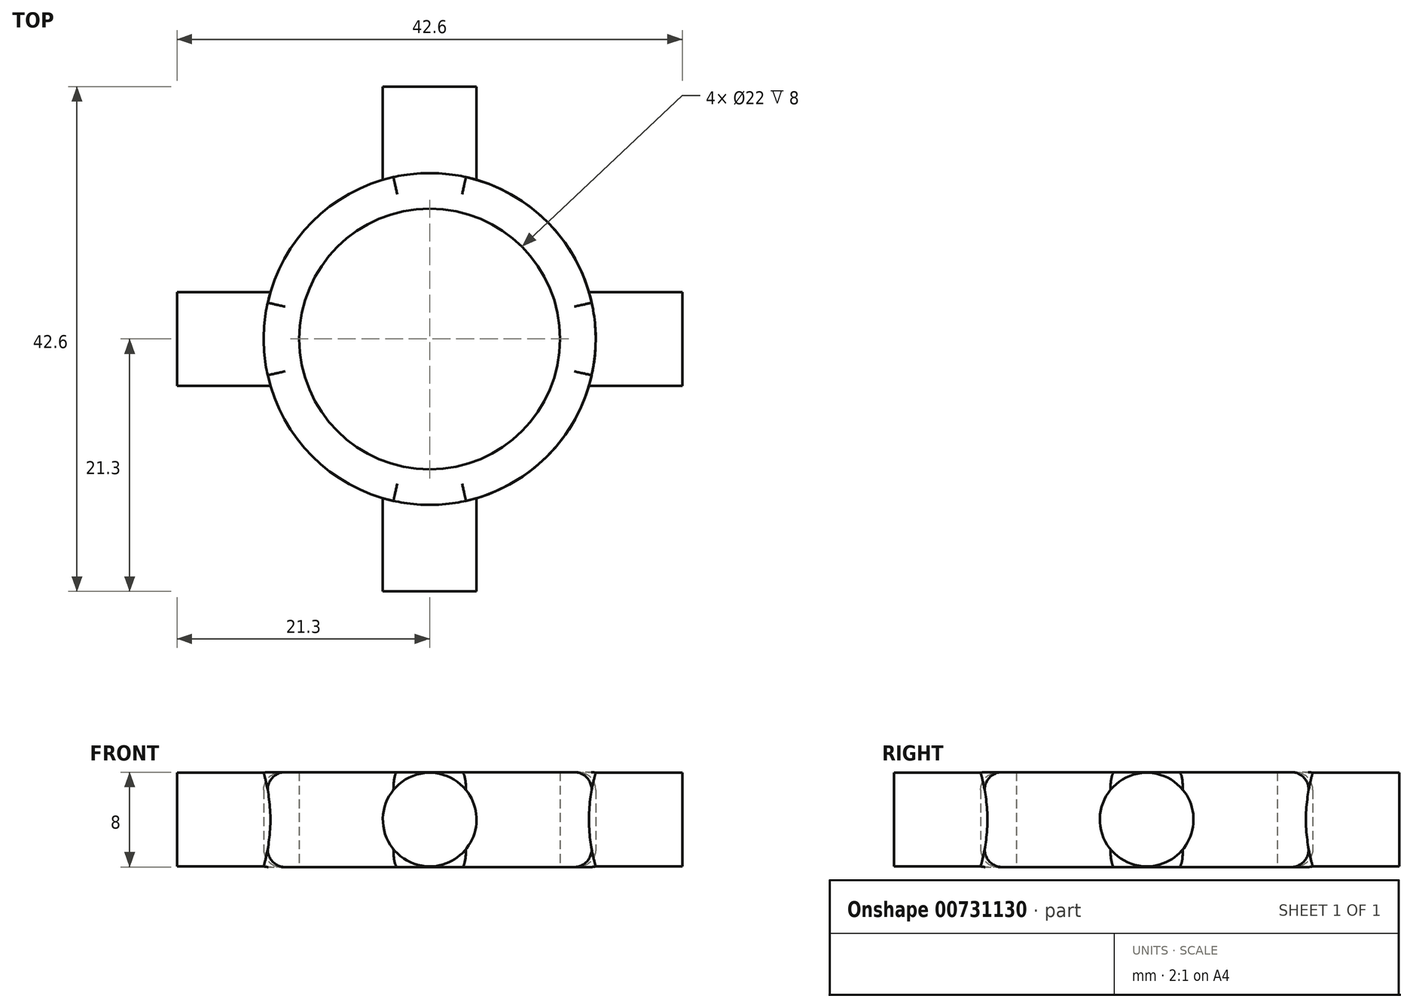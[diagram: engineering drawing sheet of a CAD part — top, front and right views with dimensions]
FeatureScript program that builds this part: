
annotation { "Feature Type Name" : "Feature", "Feature Type Description" : "" }
export const myFeature = defineFeature(function(context is Context, id is Id, definition is map)
    precondition{}
    {
        {
            var Q0;
            Q0=qCreatedBy(makeId("Top.planeOp"),FACE);
            var sketch = newSketch(context, id + "F0", { "sketchPlane" : qUnion([Q0])});
            skCircle(sketch, "E0", {"center": v(0, 0) * mm, "radius": 11 * mm});
            skCircle(sketch, "E1.0", {"center": v(0, 0) * mm, "radius": 14 * mm});
            skSolve(sketch);
        }
        {
            var Q0;
            Q0=qCreatedBy(makeId("Right.planeOp"),FACE);
            cPlane(context, id + "F1", {"entities" : qUnion([Q0]), "cplaneType" : CPlaneType.OFFSET, "offset" : 13.3 * mm, "width" : 150 * mm, "height" : 150 * mm});
        }
        {
            var Q0;
            Q0=qCreatedBy(id+"F1.planeOp",FACE);
            var sketch = newSketch(context, id + "F2", { "sketchPlane" : qUnion([Q0])});
            skCircle(sketch, "E2", {"center": v(0, 0) * mm, "radius": 3.95 * mm});
            skSolve(sketch);
        }
        {
            var Q0;
            Q0=makeQuery(id+"F0.imprint","IMPRINT",FACE,{"disambiguationData":[TD([[makeQuery(id+"F0.imprint","IMPRINT",EDGE,{"derivedFrom":sQuery(id+"F0.wireOp",EDGE,"E0")}),-1.0]])]});
            extrude(context, id + "F3", {"entities" : qUnion([Q0]), "endBound" : BoundingType.SYMMETRIC, "depth" : 8 * mm, "offsetDistance" : 25 * mm});
        }
        {
            var Q0;
            Q0=qSketchRegion(id+"F2",true);
            extrude(context, id + "F4", {"entities" : qUnion([Q0]), "operationType" : NewBodyOperationType.ADD, "depth" : 8 * mm, "offsetDistance" : 25 * mm});
        }
        {
            var Q0;
            Q0=makeQuery(id+"F3.opExtrude","CAP_EDGE",EDGE,{"disambiguationData":[OSD([sQuery(id+"F0.wireOp",EDGE,"E1.0")])],"isStart":false});
            var Q1;
            Q1=makeQuery(id+"F3.opExtrude","CAP_EDGE",EDGE,{"disambiguationData":[OSD([sQuery(id+"F0.wireOp",EDGE,"E1.0")])],"isStart":true});
            fillet(context, id + "F5", {"entities" : qUnion([Q0, Q1]), "radius" : 1.5 * mm, "tangentPropagation" : true, "allowEdgeOverflow" : false});
        }
        {
            var Q0;
            Q0=makeQuery(id+"F3.opExtrude","SWEPT_BODY",BODY,{"disambiguationData":[OSD([sQuery(id+"F0.wireOp",EDGE,"E0"),sQuery(id+"F0.wireOp",EDGE,"E1.0")])]});
            var Q1;
            Q1=makeQuery(id+"F3.opExtrude","CAP_EDGE",EDGE,{"disambiguationData":[OSD([sQuery(id+"F0.wireOp",EDGE,"E0")])],"isStart":false});
            circularPattern(context, id + "F6", {"entities" : qUnion([Q0]), "axis" : qUnion([Q1]), "angle" : 360 * degree, "instanceCount" : 4, "equalSpace" : true});
        }
    });
